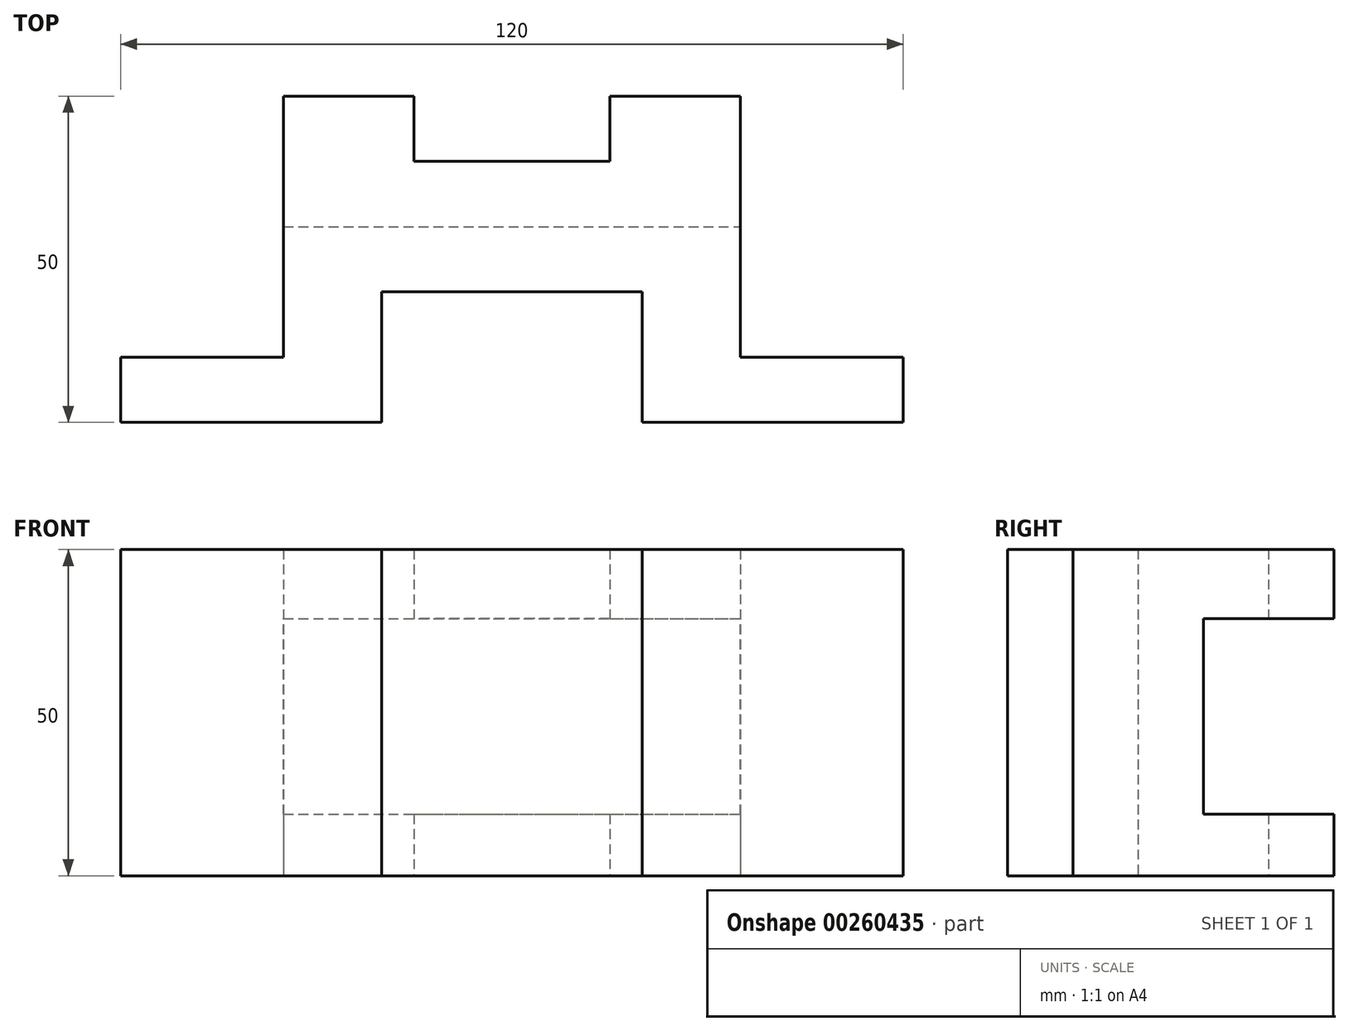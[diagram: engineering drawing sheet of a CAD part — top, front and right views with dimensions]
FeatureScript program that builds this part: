
annotation { "Feature Type Name" : "Feature", "Feature Type Description" : "" }
export const myFeature = defineFeature(function(context is Context, id is Id, definition is map)
    precondition{}
    {
        {
            var Q0;
            Q0=qCreatedBy(makeId("Top.planeOp"),FACE);
            var sketch = newSketch(context, id + "F0", { "sketchPlane" : qUnion([Q0])});
            skLineSegment(sketch, "E0", {"start": v(-48.37, 0) * mm, "end": v(-48.37, 10) * mm});
            skLineSegment(sketch, "E1", {"start": v(-48.37, 10) * mm, "end": v(-23.37, 10) * mm});
            skLineSegment(sketch, "E2", {"start": v(-23.37, 10) * mm, "end": v(-23.37, 50) * mm});
            skLineSegment(sketch, "E3", {"start": v(-23.37, 50) * mm, "end": v(-3.37, 50) * mm});
            skLineSegment(sketch, "E4", {"start": v(-3.37, 50) * mm, "end": v(-3.37, 40) * mm});
            skLineSegment(sketch, "E5", {"start": v(-3.37, 40) * mm, "end": v(26.63, 40) * mm});
            skLineSegment(sketch, "E6", {"start": v(26.63, 40) * mm, "end": v(26.63, 50) * mm});
            skLineSegment(sketch, "E7", {"start": v(26.63, 50) * mm, "end": v(46.63, 50) * mm});
            skLineSegment(sketch, "E8", {"start": v(46.63, 50) * mm, "end": v(46.63, 10) * mm});
            skLineSegment(sketch, "E9", {"start": v(46.63, 10) * mm, "end": v(71.63, 10) * mm});
            skLineSegment(sketch, "E10", {"start": v(71.63, 10) * mm, "end": v(71.63, 0) * mm});
            skLineSegment(sketch, "E11", {"start": v(71.63, 0) * mm, "end": v(31.63, 0) * mm});
            skLineSegment(sketch, "E12", {"start": v(31.63, 0) * mm, "end": v(31.63, 20) * mm});
            skLineSegment(sketch, "E13", {"start": v(31.63, 20) * mm, "end": v(-8.37, 20) * mm});
            skLineSegment(sketch, "E14", {"start": v(-8.37, 20) * mm, "end": v(-8.37, 0) * mm});
            skLineSegment(sketch, "E15", {"start": v(-8.37, 0) * mm, "end": v(-48.37, 0) * mm});
            skSolve(sketch);
        }
        {
            var Q0;
            Q0 = qSketchRegion(id + "F0", true);
            extrude(context, id + "F1", {"entities" : qUnion([Q0]), "depth" : 50 * mm});
        }
        {
            var Q0;
            Q0=makeQuery(id+"F1.opExtrude","SWEPT_FACE",FACE,{"disambiguationData":[OSD([sQuery(id+"F0.wireOp",EDGE,"E8")])]});
            var sketch = newSketch(context, id + "F2", { "sketchPlane" : qUnion([Q0])});
            skLineSegment(sketch, "E16", {"start": v(50, 9.43) * mm, "end": v(30, 9.43) * mm});
            skLineSegment(sketch, "E17", {"start": v(30, 9.43) * mm, "end": v(30, 39.43) * mm});
            skLineSegment(sketch, "E18", {"start": v(30, 39.43) * mm, "end": v(50, 39.43) * mm});
            skSolve(sketch);
        }
        {
            var Q0;
            {var subQ0=sQuery(id+"F2.wireOp",EDGE,"E16");Q0=makeQuery(id+"F2.imprint","IMPRINT",FACE,{"disambiguationData":[TD([[makeQuery(id+"F2.imprint","IMPRINT",EDGE,{"derivedFrom":subQ0}),-1.0]])]});}
            extrude(context, id + "F3", {"entities" : qUnion([Q0]), "operationType" : NewBodyOperationType.REMOVE, "oppositeDirection" : true, "depth" : 70 * mm});
        }
    });
